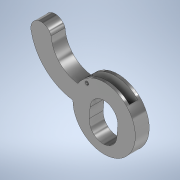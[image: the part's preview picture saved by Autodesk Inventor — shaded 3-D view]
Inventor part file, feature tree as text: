
AUTODESK INVENTOR PART (.ipt)
format: ipt  version: 2021 (Build 250183000, 183)  size: 165,376 bytes
history: native  units: mm
features: extrude x6, sketch x6, other x2
ambient origin geometry x8: Origin, YZ Plane, XZ Plane, XY Plane, X Axis, Y Axis, Z Axis, Center Point
bodies: Body1 (feature_tree)
feature tree (14):
  other  "Sólido1"
  extrude  "Extrusão1"  Depth=2.0mm TaperAngle=0.0deg
  extrude  "Extrusão2"  Depth=4.3mm
  extrude  "Extrusão3"  Depth=1.5mm
  other  "Plano de trabalho1"
  extrude  "Extrusão4"  Depth=1.5mm
  extrude  "Extrusão5"  Depth=2.0mm TaperAngle=0.0deg
  extrude  "Extrusão7"  Depth=0.4mm
  sketch  "Esboço1"  dims[d0=9.0mm d1=2.0mm d2=0.0mm]
  sketch  "Esboço2"  dims[d3=7.0mm d4=4.3mm]
  sketch  "Esboço4"  dims[d5=1.5mm d6=6.0mm]
  sketch  "Esboço5"  dims[d7=2.0mm d8=0.0mm d11=1.5mm]
  sketch  "Esboço6"  dims[d12=4.0mm d13=2.0mm d14=0.0mm]
  sketch  "Esboço8"  dims[d15=4.5mm d16=0.4mm d17=0.4mm d18=0.5mm d19=1.25mm d20=2.2mm d21=0.0mm d22=0.5mm d23=0.5mm d24=0.0mm d28=2.473mm d29=3.141mm d30=0.5mm d31=0.1mm d32=0.0mm]
